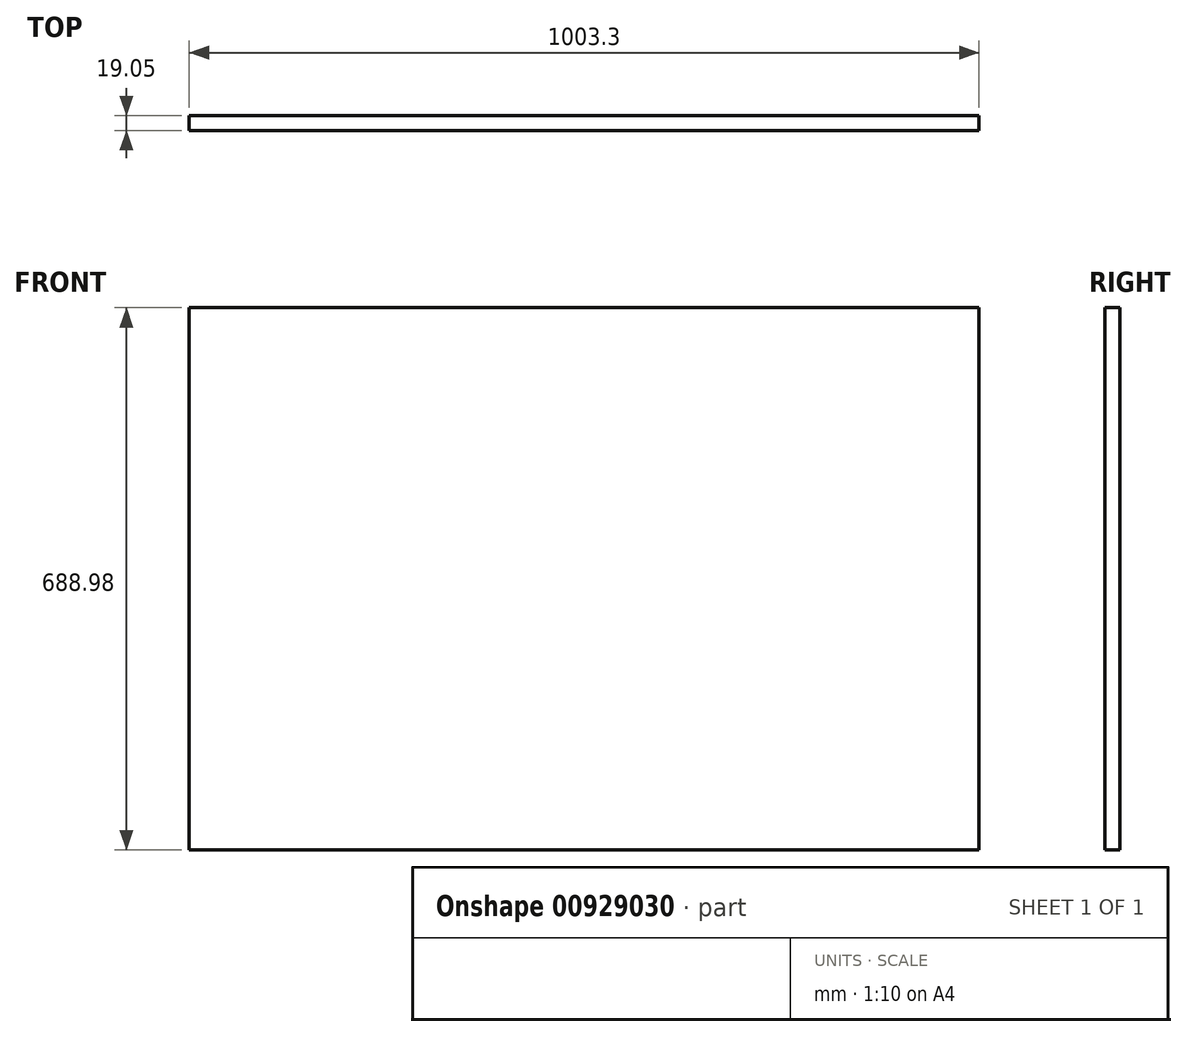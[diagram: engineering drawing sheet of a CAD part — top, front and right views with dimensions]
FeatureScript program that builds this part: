
annotation { "Feature Type Name" : "Feature", "Feature Type Description" : "" }
export const myFeature = defineFeature(function(context is Context, id is Id, definition is map)
    precondition{}
    {
        {
            var Q0;
            Q0=qCreatedBy(makeId("Front.planeOp"),FACE);
            var sketch = newSketch(context, id + "F0", { "sketchPlane" : qUnion([Q0])});
            skLineSegment(sketch, "E0.bottom", {"start": v(501.65, 344.49) * mm, "end": v(-501.65, 344.49) * mm});
            skLineSegment(sketch, "E0.top", {"start": v(501.65, -344.49) * mm, "end": v(-501.65, -344.49) * mm});
            skLineSegment(sketch, "E0.left", {"start": v(501.65, 344.49) * mm, "end": v(501.65, -344.49) * mm});
            skLineSegment(sketch, "E0.right", {"start": v(-501.65, 344.49) * mm, "end": v(-501.65, -344.49) * mm});
            skPoint(sketch, "E0.middle", {"position": v(0, 0) * mm});
            skSolve(sketch);
        }
        {
            var Q0;
            Q0=makeQuery(id+"F0.imprint","IMPRINT",FACE,{"disambiguationData":[TD([[makeQuery(id+"F0.imprint","IMPRINT",EDGE,{"derivedFrom":sQuery(id+"F0.wireOp",EDGE,"E0.bottom")}),1.0]])]});
            extrude(context, id + "F1", {"entities" : qUnion([Q0]), "depth" : 19.05 * mm, "offsetDistance" : 25.4 * mm});
        }
    });
